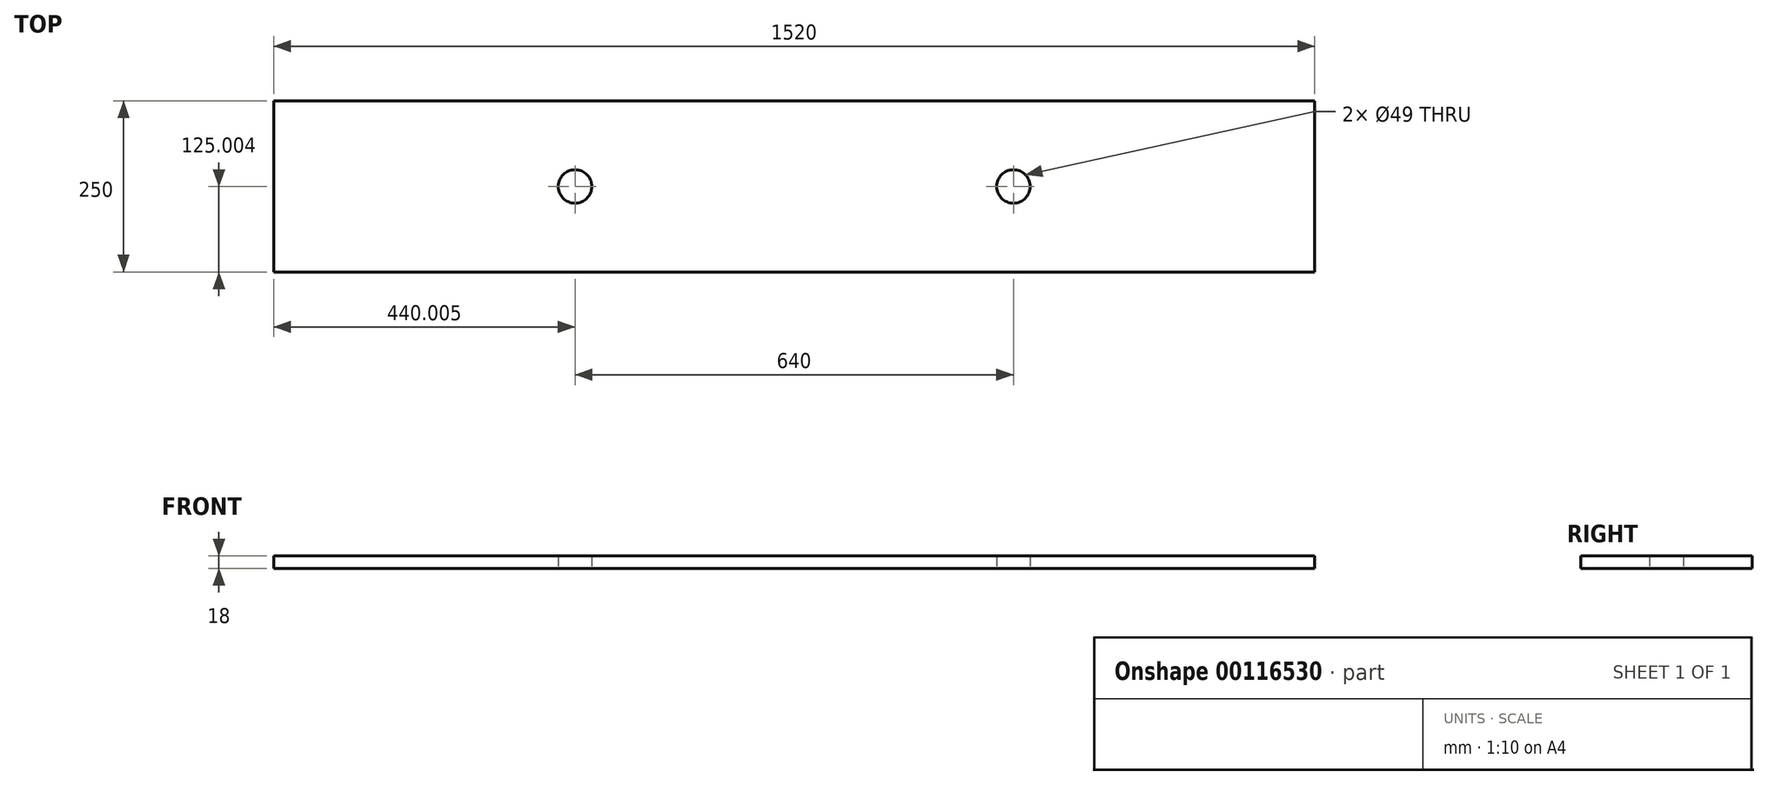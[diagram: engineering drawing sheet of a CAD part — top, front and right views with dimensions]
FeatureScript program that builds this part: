
annotation { "Feature Type Name" : "Feature", "Feature Type Description" : "" }
export const myFeature = defineFeature(function(context is Context, id is Id, definition is map)
    precondition{}
    {
        {
            var Q0;
            Q0=qCreatedBy(makeId("Top.planeOp"),FACE);
            var sketch = newSketch(context, id + "F0", { "sketchPlane" : qUnion([Q0])});
            skLineSegment(sketch, "E0.bottom", {"start": v(-57.48, 285.12) * mm, "end": v(1462.52, 285.12) * mm});
            skLineSegment(sketch, "E0.top", {"start": v(-57.48, 35.12) * mm, "end": v(1462.52, 35.12) * mm});
            skLineSegment(sketch, "E0.left", {"start": v(-57.48, 285.12) * mm, "end": v(-57.48, 35.12) * mm});
            skLineSegment(sketch, "E0.right", {"start": v(1462.52, 285.12) * mm, "end": v(1462.52, 35.12) * mm});
            skLineSegment(sketch, "E1", {"start": v(-57.48, 160.12) * mm, "end": v(1462.52, 160.12) * mm, "construction": true});
            skCircle(sketch, "E2", {"center": v(1022.52, 160.12) * mm, "radius": 24.5 * mm});
            skCircle(sketch, "E3", {"center": v(382.52, 160.12) * mm, "radius": 24.5 * mm});
            skSolve(sketch);
        }
        {
            var Q0;
            Q0=makeQuery(id+"F0.imprint","IMPRINT",FACE,{"disambiguationData":[TD([[makeQuery(id+"F0.imprint","IMPRINT",EDGE,{"derivedFrom":sQuery(id+"F0.wireOp",EDGE,"E0.bottom")}),-1.0]])]});
            var Q1;
            Q1=makeQuery(id+"F0.imprint","IMPRINT",FACE,{"disambiguationData":[TD([[makeQuery(id+"F0.imprint","IMPRINT",EDGE,{"derivedFrom":sQuery(id+"F0.wireOp",EDGE,"E0.bottom")}),-1.0]])]});
            var Q2;
            {var subQ0=sQuery(id+"F0.wireOp",EDGE,"E0.left");Q2=makeQuery(id+"F0.imprint","IMPRINT",FACE,{"disambiguationData":[TD([[makeQuery(id+"F0.imprint","IMPRINT",EDGE,{"derivedFrom":subQ0}),1.0]])]});}
            extrude(context, id + "F1", {"entities" : qUnion([Q0, Q1, Q2]), "depth" : 18 * mm});
        }
    });
